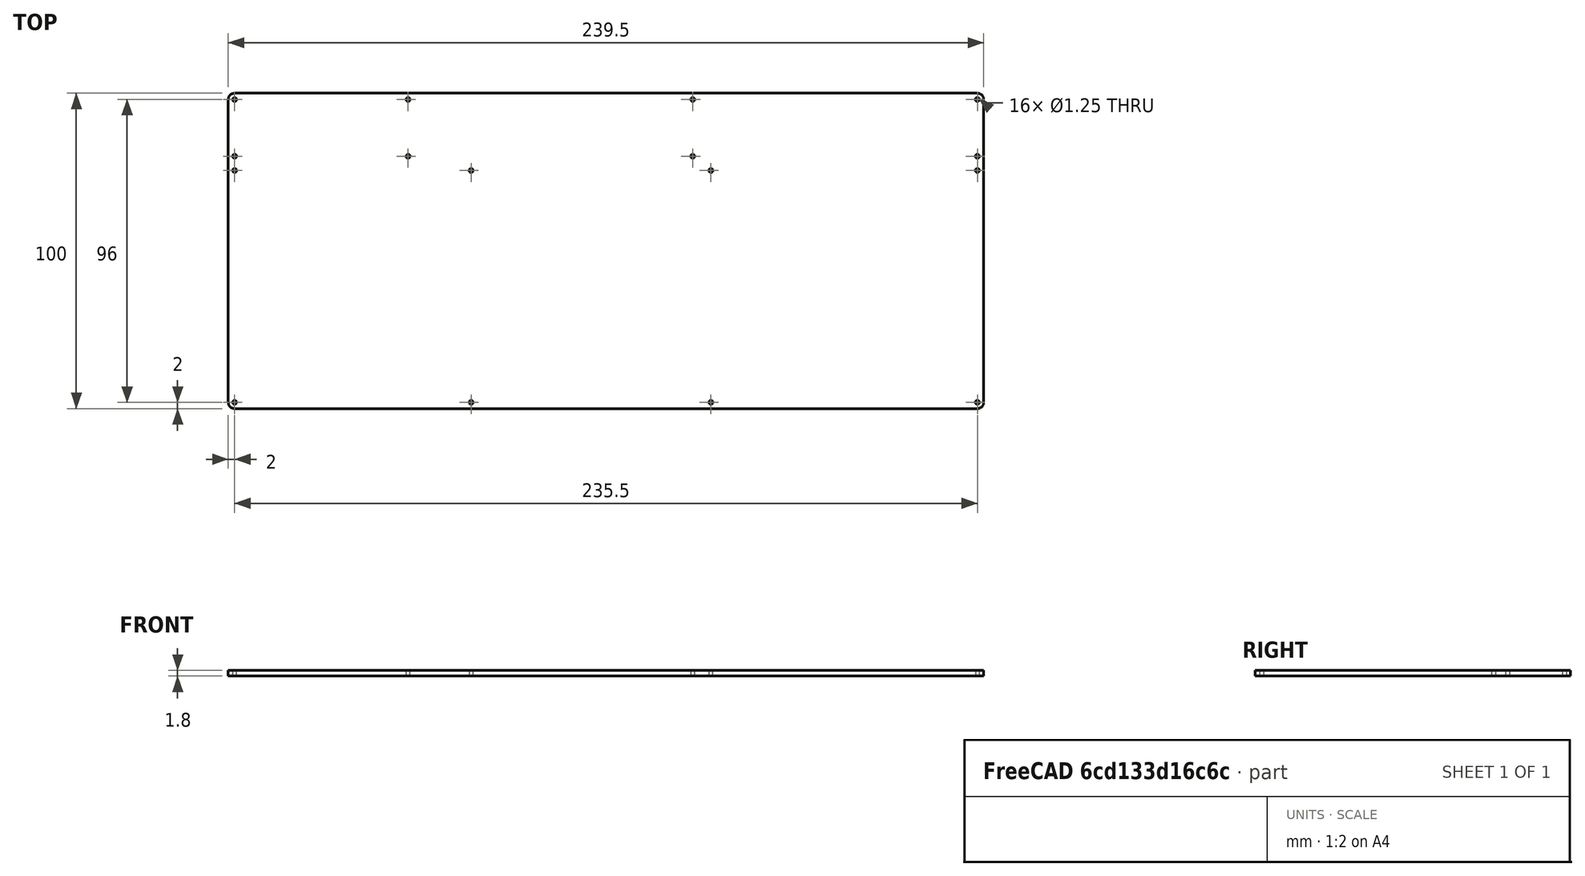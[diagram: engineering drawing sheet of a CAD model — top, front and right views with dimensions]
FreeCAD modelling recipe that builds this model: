
FCSTD DOCUMENT  (FreeCAD 1.0R39285 (Git))
Label: back-plate
License: All rights reserved
LicenseURL: https://en.wikipedia.org/wiki/All_rights_reserved
objects: Sketcher::SketchObject×1, PartDesign::Pad×1, PartDesign::Body×1
note: 6 computed .brp shape members not serialized (recipe doc carries the construction recipe); baked Part::Feature solids carry a one-line shape summary decoded from their .brp

FEATURE [Sketcher::SketchObject] Sketch
  ArcFitTolerance = 1e-06
  AttachmentSupport = -> [XY_Plane]
  FullyConstrained = true
  MakeInternals = false
  MapMode = 5
  sketch-geometry (28):
    g0: LineSegment StartX=-119.75 StartY=48 StartZ=0 EndX=-119.75 EndY=-48 EndZ=0
    g1: LineSegment StartX=-117.75 StartY=-50 StartZ=0 EndX=117.75 EndY=-50 EndZ=0
    g2: LineSegment StartX=119.75 StartY=-48 StartZ=0 EndX=119.75 EndY=48 EndZ=0
    g3: LineSegment StartX=117.75 StartY=50 StartZ=0 EndX=-117.75 EndY=50 EndZ=0
    g4: ArcOfCircle CenterX=117.75 CenterY=48 CenterZ=0 NormalX=0 NormalY=0 NormalZ=1 AngleXU=0 Radius=2 StartAngle=1e-16 EndAngle=1.5708
    g5: GeomPoint [constr] X=119.75 Y=50 Z=0
    g6: ArcOfCircle CenterX=117.75 CenterY=-48 CenterZ=0 NormalX=0 NormalY=0 NormalZ=1 AngleXU=0 Radius=2 StartAngle=4.71239 EndAngle=6.28319
    g7: GeomPoint [constr] X=119.75 Y=-50 Z=0
    g8: ArcOfCircle CenterX=-117.75 CenterY=-48 CenterZ=0 NormalX=0 NormalY=0 NormalZ=1 AngleXU=0 Radius=2 StartAngle=3.14159 EndAngle=4.71239
    g9: GeomPoint [constr] X=-119.75 Y=-50 Z=0
    g10: ArcOfCircle CenterX=-117.75 CenterY=48 CenterZ=0 NormalX=0 NormalY=0 NormalZ=1 AngleXU=0 Radius=2 StartAngle=1.5708 EndAngle=3.14159
    g11: GeomPoint [constr] X=-119.75 Y=50 Z=0
    g12: Circle CenterX=-117.75 CenterY=48 CenterZ=0 NormalX=0 NormalY=0 NormalZ=1 AngleXU=0 Radius=0.625
    g13: Circle CenterX=117.75 CenterY=48 CenterZ=0 NormalX=0 NormalY=0 NormalZ=1 AngleXU=0 Radius=0.625
    g14: Circle CenterX=117.75 CenterY=-48 CenterZ=0 NormalX=0 NormalY=0 NormalZ=1 AngleXU=0 Radius=0.625
    g15: Circle CenterX=-117.75 CenterY=-48 CenterZ=0 NormalX=0 NormalY=0 NormalZ=1 AngleXU=0 Radius=0.625
    g16: Circle CenterX=-117.75 CenterY=30 CenterZ=0 NormalX=0 NormalY=0 NormalZ=1 AngleXU=0 Radius=0.625
    g17: Circle CenterX=-62.75 CenterY=48 CenterZ=0 NormalX=0 NormalY=0 NormalZ=1 AngleXU=0 Radius=0.625
    g18: Circle CenterX=-62.75 CenterY=30 CenterZ=0 NormalX=0 NormalY=0 NormalZ=1 AngleXU=0 Radius=0.625
    g19: Circle CenterX=27.5 CenterY=48 CenterZ=0 NormalX=0 NormalY=0 NormalZ=1 AngleXU=0 Radius=0.625
    g20: Circle CenterX=33.25 CenterY=-48 CenterZ=0 NormalX=0 NormalY=0 NormalZ=1 AngleXU=0 Radius=0.625
    g21: Circle CenterX=-42.75 CenterY=-48 CenterZ=0 NormalX=0 NormalY=0 NormalZ=1 AngleXU=0 Radius=0.625
    g22: Circle CenterX=117.75 CenterY=30 CenterZ=0 NormalX=0 NormalY=0 NormalZ=1 AngleXU=0 Radius=0.625
    g23: Circle CenterX=117.75 CenterY=25.5 CenterZ=0 NormalX=0 NormalY=0 NormalZ=1 AngleXU=0 Radius=0.625
    g24: Circle CenterX=27.5 CenterY=30 CenterZ=0 NormalX=0 NormalY=0 NormalZ=1 AngleXU=0 Radius=0.625
    g25: Circle CenterX=-117.75 CenterY=25.5 CenterZ=0 NormalX=0 NormalY=0 NormalZ=1 AngleXU=0 Radius=0.625
    g26: Circle CenterX=33.25 CenterY=25.5 CenterZ=0 NormalX=0 NormalY=0 NormalZ=1 AngleXU=0 Radius=0.625
    g27: Circle CenterX=-42.75 CenterY=25.5 CenterZ=0 NormalX=0 NormalY=0 NormalZ=1 AngleXU=0 Radius=0.625
  constraints (71):
    c: Vertical(g0)
    c: Vertical(g2)
    c: Horizontal(g1)
    c: Horizontal(g3)
    c: DistanceY(g9,g11) = 100
    c: DistanceX(g11,g5) = 239.5
    c: Symmetric(g11,g7,g-1)
    c: PointOnObject(g5,g3)
    c: PointOnObject(g5,g2)
    c: Tangent(g3,g4) = -1.5708
    c: Tangent(g2,g4) = -1.5708
    c: PointOnObject(g7,g2)
    c: PointOnObject(g7,g1)
    c: Tangent(g2,g6) = -1.5708
    c: Tangent(g1,g6) = -1.5708
    c: PointOnObject(g9,g1)
    c: PointOnObject(g9,g0)
    c: Tangent(g1,g8) = -1.5708
    c: Tangent(g0,g8) = -1.5708
    c: PointOnObject(g11,g0)
    c: PointOnObject(g11,g3)
    c: Tangent(g0,g10) = -1.5708
    c: Tangent(g3,g10) = -1.5708
    c: Radius(g10) = 2
    c: Equal(g6,g4)
    c: Equal(g4,g8)
    c: Equal(g8,g10)
    c: Diameter(g12) = 1.25
    c: Coincident(g12,g10)
    c: Equal(g12,g15)
    c: Equal(g15,g14)
    c: Equal(g14,g13)
    c: Coincident(g15,g8)
    c: Coincident(g13,g4)
    c: Coincident(g14,g6)
    c: Horizontal(g10,g17)
    c: Horizontal(g17,g19)
    c: Vertical(g10,g25)
    c: Vertical(g25,g16)
    c: Vertical(g22,g23)
    c: Vertical(g23,g4)
    c: Horizontal(g21,g20)
    c: Horizontal(g20,g8)
    c: Equal(g12,g16)
    c: Equal(g12,g25)
    c: Equal(g25,g17)
    c: Equal(g17,g18)
    c: Equal(g12,g19)
    c: Equal(g19,g24)
    c: Equal(g24,g27)
    c: Equal(g27,g26)
    c: Equal(g26,g21)
    c: Equal(g21,g20)
    c: Equal(g20,g23)
    c: Equal(g23,g22)
    c: Horizontal(g16,g18)
    c: Horizontal(g18,g24)
    c: Horizontal(g24,g22)
    c: Horizontal(g25,g27)
    c: Horizontal(g27,g26)
    c: Horizontal(g26,g23)
    c: Vertical(g17,g18)
    c: Vertical(g24,g19)
    c: Vertical(g26,g20)
    c: Vertical(g27,g21)
    c: DistanceX(g10,g17) = 55
    c: DistanceY(g16,g10) = 18
    c: Distance(g25,g16) = 4.5
    c: DistanceX(g8,g21) = 75
    c: DistanceX(g17,g19) = 90.25
    c: DistanceX(g21,g20) = 76
FEATURE [PartDesign::Pad] Pad
  Direction = (0,0,1)
  Length = 1.8
  Length2 = 10
  Profile = -> Sketch
  ReferenceAxis = -> Sketch [N_Axis]
  Refine = true
  Suppressed = false
  Type = 0
FEATURE [PartDesign::Body] Body
  AllowCompound = false
  Group = -> [Sketch,Pad]
  Origin = -> Origin
  Tip = -> Pad
